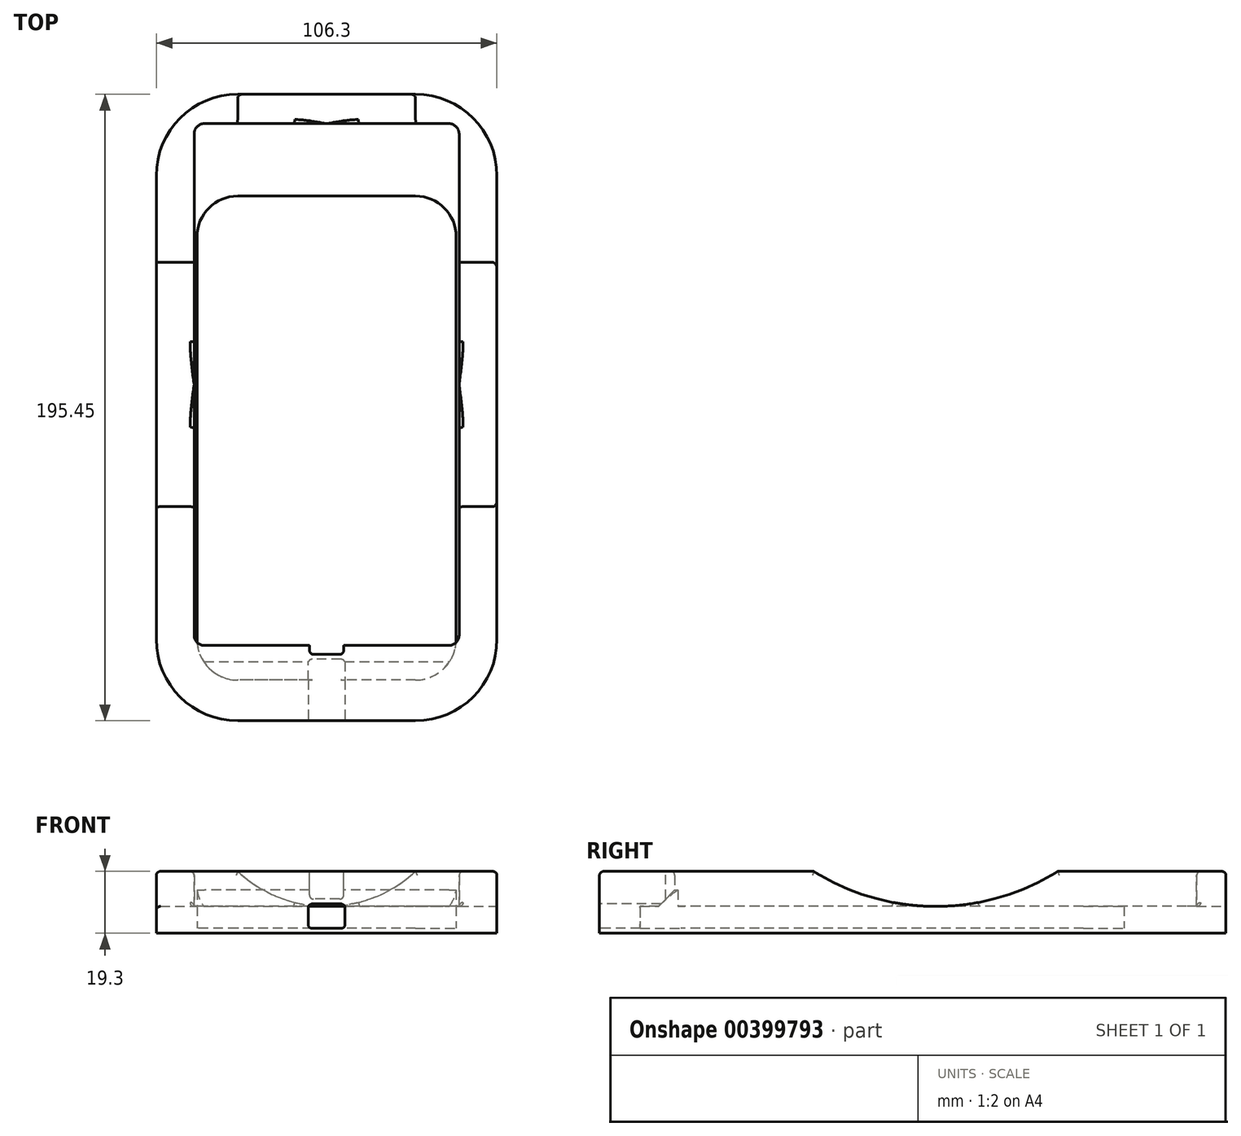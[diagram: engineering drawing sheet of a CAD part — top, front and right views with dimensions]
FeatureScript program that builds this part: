
annotation { "Feature Type Name" : "Feature", "Feature Type Description" : "" }
export const myFeature = defineFeature(function(context is Context, id is Id, definition is map)
    precondition{}
    {
        {
            var Q0;
            Q0=qCreatedBy(makeId("Top.planeOp"),FACE);
            var sketch = newSketch(context, id + "F0", { "sketchPlane" : qUnion([Q0])});
            skLineSegment(sketch, "E0.bottom", {"start": v(27.75, 75.5) * mm, "end": v(-27.75, 75.5) * mm});
            skLineSegment(sketch, "E0.top", {"start": v(27.75, -75.5) * mm, "end": v(-27.75, -75.5) * mm});
            skLineSegment(sketch, "E0.left", {"start": v(40.45, 62.8) * mm, "end": v(40.45, -62.8) * mm});
            skLineSegment(sketch, "E0.right", {"start": v(-40.45, 62.8) * mm, "end": v(-40.45, -62.8) * mm});
            skPoint(sketch, "E0.middle", {"position": v(0, 0) * mm});
            skPoint(sketch, "E1.visualSharp", {"position": v(40.45, 75.5) * mm});
            skArc(sketch, "E1.filletArc", {"start": v(40.45, 62.8) * mm, "mid": v(36.73, 71.78) * mm, "end": v(27.75, 75.5) * mm});
            skPoint(sketch, "E2.visualSharp", {"position": v(-40.45, 75.5) * mm});
            skArc(sketch, "E2.filletArc", {"start": v(-27.75, 75.5) * mm, "mid": v(-36.73, 71.78) * mm, "end": v(-40.45, 62.8) * mm});
            skPoint(sketch, "E3.visualSharp", {"position": v(-40.45, -75.5) * mm});
            skArc(sketch, "E3.filletArc", {"start": v(-40.45, -62.8) * mm, "mid": v(-36.73, -71.78) * mm, "end": v(-27.75, -75.5) * mm});
            skPoint(sketch, "E4.visualSharp", {"position": v(40.45, -75.5) * mm});
            skArc(sketch, "E4.filletArc", {"start": v(27.75, -75.5) * mm, "mid": v(36.73, -71.78) * mm, "end": v(40.45, -62.8) * mm});
            skLineSegment(sketch, "E5.0", {"start": v(-53.15, 81.85) * mm, "end": v(-53.15, -62.8) * mm});
            skLineSegment(sketch, "E5.1", {"start": v(53.15, 81.85) * mm, "end": v(53.15, -62.8) * mm});
            skArc(sketch, "E5.2", {"start": v(27.75, -88.2) * mm, "mid": v(45.71, -80.76) * mm, "end": v(53.15, -62.8) * mm});
            skLineSegment(sketch, "E5.3", {"start": v(27.75, -88.2) * mm, "end": v(-27.75, -88.2) * mm});
            skArc(sketch, "E5.4", {"start": v(-53.15, -62.8) * mm, "mid": v(-45.71, -80.76) * mm, "end": v(-27.75, -88.2) * mm});
            skLineSegment(sketch, "E6", {"start": v(-27.75, 107.25) * mm, "end": v(27.75, 107.25) * mm});
            skPoint(sketch, "E7.visualSharp", {"position": v(53.15, 107.25) * mm});
            skArc(sketch, "E7.filletArc", {"start": v(53.15, 81.85) * mm, "mid": v(45.71, 99.81) * mm, "end": v(27.75, 107.25) * mm});
            skPoint(sketch, "E8.visualSharp", {"position": v(-53.15, 107.25) * mm});
            skArc(sketch, "E8.filletArc", {"start": v(-27.75, 107.25) * mm, "mid": v(-45.71, 99.81) * mm, "end": v(-53.15, 81.85) * mm});
            skSolve(sketch);
        }
        {
            var Q0;
            Q0 = qSketchRegion(id + "F0", true);
            var Q1;
            Q1=makeQuery(id+"F0.imprint","IMPRINT",FACE,{"disambiguationData":[TD([[makeQuery(id+"F0.imprint","IMPRINT",EDGE,{"derivedFrom":sQuery(id+"F0.wireOp",EDGE,"E0.bottom")}),1.0]])]});
            extrude(context, id + "F1", {"entities" : qUnion([Q0, Q1]), "depth" : 1.52 * mm});
        }
        {
            var Q0;
            Q0=makeQuery(id+"F1.opExtrude","CAP_FACE",FACE,{"disambiguationData":[OSD([sQuery(id+"F0.wireOp",EDGE,"E5.0"),sQuery(id+"F0.wireOp",EDGE,"E5.1"),sQuery(id+"F0.wireOp",EDGE,"E5.2"),sQuery(id+"F0.wireOp",EDGE,"E5.3"),sQuery(id+"F0.wireOp",EDGE,"E5.4"),sQuery(id+"F0.wireOp",EDGE,"E6"),sQuery(id+"F0.wireOp",EDGE,"E7.filletArc"),sQuery(id+"F0.wireOp",EDGE,"E8.filletArc")])],"isStart":false});
            var sketch = newSketch(context, id + "F2", { "sketchPlane" : qUnion([Q0])});
            skLineSegment(sketch, "E9.0", {"start": v(27.75, 75.5) * mm, "end": v(-27.75, 75.5) * mm});
            skLineSegment(sketch, "E9.1", {"start": v(27.75, -75.5) * mm, "end": v(-27.75, -75.5) * mm});
            skLineSegment(sketch, "E9.2", {"start": v(40.45, 62.8) * mm, "end": v(40.45, -62.8) * mm});
            skLineSegment(sketch, "E9.3", {"start": v(-40.45, 62.8) * mm, "end": v(-40.45, -62.8) * mm});
            skPoint(sketch, "E9.4", {"position": v(0, 0) * mm});
            skPoint(sketch, "E9.5", {"position": v(40.45, 75.5) * mm});
            skArc(sketch, "E9.6", {"start": v(40.45, 62.8) * mm, "mid": v(36.73, 71.78) * mm, "end": v(27.75, 75.5) * mm});
            skPoint(sketch, "E9.7", {"position": v(-40.45, 75.5) * mm});
            skArc(sketch, "E9.8", {"start": v(-27.75, 75.5) * mm, "mid": v(-36.73, 71.78) * mm, "end": v(-40.45, 62.8) * mm});
            skPoint(sketch, "E9.9", {"position": v(-40.45, -75.5) * mm});
            skArc(sketch, "E9.10", {"start": v(-40.45, -62.8) * mm, "mid": v(-36.73, -71.78) * mm, "end": v(-27.75, -75.5) * mm});
            skPoint(sketch, "E9.11", {"position": v(40.45, -75.5) * mm});
            skArc(sketch, "E9.12", {"start": v(27.75, -75.5) * mm, "mid": v(36.73, -71.78) * mm, "end": v(40.45, -62.8) * mm});
            skLineSegment(sketch, "E9.13", {"start": v(-53.15, 81.85) * mm, "end": v(-53.15, -62.8) * mm});
            skLineSegment(sketch, "E9.14", {"start": v(53.15, 81.85) * mm, "end": v(53.15, -62.8) * mm});
            skArc(sketch, "E9.15", {"start": v(27.75, -88.2) * mm, "mid": v(45.71, -80.76) * mm, "end": v(53.15, -62.8) * mm});
            skLineSegment(sketch, "E9.16", {"start": v(27.75, -88.2) * mm, "end": v(-27.75, -88.2) * mm});
            skArc(sketch, "E9.17", {"start": v(-53.15, -62.8) * mm, "mid": v(-45.71, -80.76) * mm, "end": v(-27.75, -88.2) * mm});
            skLineSegment(sketch, "E9.18", {"start": v(-27.75, 107.25) * mm, "end": v(27.75, 107.25) * mm});
            skPoint(sketch, "E9.19", {"position": v(53.15, 107.25) * mm});
            skArc(sketch, "E9.20", {"start": v(53.15, 81.85) * mm, "mid": v(45.71, 99.81) * mm, "end": v(27.75, 107.25) * mm});
            skPoint(sketch, "E9.21", {"position": v(-53.15, 107.25) * mm});
            skArc(sketch, "E9.22", {"start": v(-27.75, 107.25) * mm, "mid": v(-45.71, 99.81) * mm, "end": v(-53.15, 81.85) * mm});
            skSolve(sketch);
        }
        {
            var Q0;
            Q0 = qSketchRegion(id + "F2", true);
            extrude(context, id + "F3", {"entities" : qUnion([Q0]), "operationType" : NewBodyOperationType.ADD, "depth" : 6.86 * mm});
        }
        {
            var Q0;
            Q0=makeQuery(id+"F3.opExtrude","CAP_FACE",FACE,{"disambiguationData":[OSD([sQuery(id+"F2.wireOp",EDGE,"E9.0"),sQuery(id+"F2.wireOp",EDGE,"E9.1"),sQuery(id+"F2.wireOp",EDGE,"E9.2"),sQuery(id+"F2.wireOp",EDGE,"E9.3"),sQuery(id+"F2.wireOp",EDGE,"E9.6"),sQuery(id+"F2.wireOp",EDGE,"E9.8"),sQuery(id+"F2.wireOp",EDGE,"E9.10"),sQuery(id+"F2.wireOp",EDGE,"E9.12"),sQuery(id+"F2.wireOp",EDGE,"E9.13"),sQuery(id+"F2.wireOp",EDGE,"E9.14"),sQuery(id+"F2.wireOp",EDGE,"E9.15"),sQuery(id+"F2.wireOp",EDGE,"E9.16"),sQuery(id+"F2.wireOp",EDGE,"E9.17"),sQuery(id+"F2.wireOp",EDGE,"E9.18"),sQuery(id+"F2.wireOp",EDGE,"E9.20"),sQuery(id+"F2.wireOp",EDGE,"E9.22")])],"isStart":false});
            var sketch = newSketch(context, id + "F4", { "sketchPlane" : qUnion([Q0])});
            skLineSegment(sketch, "E10.0", {"start": v(-27.75, 107.25) * mm, "end": v(27.75, 107.25) * mm});
            skArc(sketch, "E10.1", {"start": v(53.15, 81.85) * mm, "mid": v(45.71, 99.81) * mm, "end": v(27.75, 107.25) * mm});
            skLineSegment(sketch, "E10.2", {"start": v(53.15, 81.85) * mm, "end": v(53.15, -62.8) * mm});
            skArc(sketch, "E10.3", {"start": v(-27.75, 107.25) * mm, "mid": v(-45.71, 99.81) * mm, "end": v(-53.15, 81.85) * mm});
            skLineSegment(sketch, "E10.4", {"start": v(-53.15, 81.85) * mm, "end": v(-53.15, -62.8) * mm});
            skArc(sketch, "E10.5", {"start": v(-53.15, -62.8) * mm, "mid": v(-45.71, -80.76) * mm, "end": v(-27.75, -88.2) * mm});
            skLineSegment(sketch, "E10.6", {"start": v(27.75, -88.2) * mm, "end": v(-27.75, -88.2) * mm});
            skArc(sketch, "E10.7", {"start": v(27.75, -88.2) * mm, "mid": v(45.71, -80.76) * mm, "end": v(53.15, -62.8) * mm});
            skLineSegment(sketch, "E11.bottom", {"start": v(38.16, 98.1) * mm, "end": v(-38.16, 98.1) * mm});
            skLineSegment(sketch, "E11.top", {"start": v(38.16, -64.7) * mm, "end": v(-38.16, -64.7) * mm});
            skLineSegment(sketch, "E11.left", {"start": v(41.34, 94.93) * mm, "end": v(41.34, -61.53) * mm});
            skLineSegment(sketch, "E11.right", {"start": v(-41.34, 94.93) * mm, "end": v(-41.34, -61.53) * mm});
            skPoint(sketch, "E11.middle", {"position": v(0, 16.7) * mm});
            skPoint(sketch, "E12.visualSharp", {"position": v(-41.34, 98.1) * mm});
            skArc(sketch, "E12.filletArc", {"start": v(-38.16, 98.1) * mm, "mid": v(-40.4, 97.18) * mm, "end": v(-41.34, 94.93) * mm});
            skPoint(sketch, "E13.visualSharp", {"position": v(41.34, 98.1) * mm});
            skArc(sketch, "E13.filletArc", {"start": v(41.34, 94.93) * mm, "mid": v(40.4, 97.18) * mm, "end": v(38.16, 98.1) * mm});
            skArc(sketch, "E14.filletArc", {"start": v(-41.34, -61.53) * mm, "mid": v(-40.4, -63.78) * mm, "end": v(-38.16, -64.7) * mm});
            skPoint(sketch, "E15.visualSharp", {"position": v(41.34, -64.7) * mm});
            skArc(sketch, "E15.filletArc", {"start": v(38.16, -64.7) * mm, "mid": v(40.4, -63.78) * mm, "end": v(41.34, -61.53) * mm});
            skSolve(sketch);
        }
        {
            var Q0;
            Q0 = qSketchRegion(id + "F4", true);
            extrude(context, id + "F5", {"entities" : qUnion([Q0]), "operationType" : NewBodyOperationType.ADD, "depth" : 10.92 * mm});
        }
        {
            var Q0;
            Q0=makeQuery(id+"F5.opExtrude","CAP_EDGE",EDGE,{"disambiguationData":[OSD([sQuery(id+"F4.wireOp",EDGE,"E11.top")])],"isStart":true});
            chamfer(context, id + "F6", {"entities" : qUnion([Q0]), "width" : 5.08 * mm, "tangentPropagation" : true});
        }
        {
            var Q0;
            Q0=makeQuery(id+"F5.opExtrude","CAP_FACE",FACE,{"disambiguationData":[OSD([sQuery(id+"F4.wireOp",EDGE,"E10.0"),sQuery(id+"F4.wireOp",EDGE,"E10.1"),sQuery(id+"F4.wireOp",EDGE,"E10.2"),sQuery(id+"F4.wireOp",EDGE,"E10.3"),sQuery(id+"F4.wireOp",EDGE,"E10.4"),sQuery(id+"F4.wireOp",EDGE,"E10.5"),sQuery(id+"F4.wireOp",EDGE,"E10.6"),sQuery(id+"F4.wireOp",EDGE,"E10.7"),sQuery(id+"F4.wireOp",EDGE,"E11.bottom"),sQuery(id+"F4.wireOp",EDGE,"E11.top"),sQuery(id+"F4.wireOp",EDGE,"E11.left"),sQuery(id+"F4.wireOp",EDGE,"E11.right"),sQuery(id+"F4.wireOp",EDGE,"E12.filletArc"),sQuery(id+"F4.wireOp",EDGE,"E13.filletArc"),sQuery(id+"F4.wireOp",EDGE,"E14.filletArc"),sQuery(id+"F4.wireOp",EDGE,"E15.filletArc")])],"isStart":false});
            var sketch = newSketch(context, id + "F7", { "sketchPlane" : qUnion([Q0])});
            skLineSegment(sketch, "E16", {"start": v(0, 0) * mm, "end": v(0, -97.5) * mm, "construction": true});
            skPoint(sketch, "E16.endSnap0", {"position": v(0, -88.2) * mm});
            skLineSegment(sketch, "E17.bottom", {"start": v(5.33, -67.5) * mm, "end": v(-5.33, -67.5) * mm});
            skLineSegment(sketch, "E17.top", {"start": v(5.33, -44.94) * mm, "end": v(-5.33, -44.94) * mm});
            skLineSegment(sketch, "E17.left", {"start": v(5.33, -67.5) * mm, "end": v(5.33, -44.94) * mm});
            skLineSegment(sketch, "E17.right", {"start": v(-5.33, -67.5) * mm, "end": v(-5.33, -44.94) * mm});
            skPoint(sketch, "E17.middle", {"position": v(0, -56.22) * mm});
            skSolve(sketch);
        }
        {
            var Q0;
            Q0 = qSketchRegion(id + "F7", true);
            var Q1;
            Q1=makeQuery(id+"F1.opExtrude","CAP_FACE",FACE,{"disambiguationData":[OSD([sQuery(id+"F0.wireOp",EDGE,"E5.0"),sQuery(id+"F0.wireOp",EDGE,"E5.1"),sQuery(id+"F0.wireOp",EDGE,"E5.2"),sQuery(id+"F0.wireOp",EDGE,"E5.3"),sQuery(id+"F0.wireOp",EDGE,"E5.4"),sQuery(id+"F0.wireOp",EDGE,"E6"),sQuery(id+"F0.wireOp",EDGE,"E7.filletArc"),sQuery(id+"F0.wireOp",EDGE,"E8.filletArc")])],"isStart":false});
            extrude(context, id + "F8", {"entities" : qUnion([Q0]), "operationType" : NewBodyOperationType.REMOVE, "endBound" : BoundingType.UP_TO_SURFACE, "oppositeDirection" : true, "endBoundEntityFace" : qUnion([Q1]), "depth" : 25.4 * mm});
        }
        {
            var Q0;
            Q0=makeQuery(id+"F8.boolean.opBoolean","COPY",EDGE,{"derivedFrom":makeQuery(id+"F8.opExtrude","SWEPT_EDGE",EDGE,{"disambiguationData":[OSD([sQuery(id+"F7.wireOp",EDGE,"E17.bottom"),sQuery(id+"F7.wireOp",EDGE,"E17.left")])]})});
            var Q1;
            Q1=makeQuery(id+"F8.boolean.opBoolean","COPY",EDGE,{"derivedFrom":makeQuery(id+"F8.opExtrude","SWEPT_EDGE",EDGE,{"disambiguationData":[OSD([sQuery(id+"F7.wireOp",EDGE,"E17.bottom"),sQuery(id+"F7.wireOp",EDGE,"E17.right")])]})});
            fillet(context, id + "F9", {"entities" : qUnion([Q0, Q1]), "radius" : 1.27 * mm, "tangentPropagation" : true, "allowEdgeOverflow" : false});
        }
        {
            var Q0;
            Q0=makeQuery(id+"F5.boolean.opBoolean","MERGE",FACE,{"derivedFrom":[makeQuery(id+"F3.boolean.opBoolean","MERGE",FACE,{"derivedFrom":[makeQuery(id+"F1.opExtrude","SWEPT_FACE",FACE,{"disambiguationData":[OSD([sQuery(id+"F0.wireOp",EDGE,"E5.3")])]}),makeQuery(id+"F3.opExtrude","SWEPT_FACE",FACE,{"disambiguationData":[OSD([sQuery(id+"F2.wireOp",EDGE,"E9.16")])]})]}),makeQuery(id+"F5.opExtrude","SWEPT_FACE",FACE,{"disambiguationData":[OSD([sQuery(id+"F4.wireOp",EDGE,"E10.6")])]})]});
            var sketch = newSketch(context, id + "F10", { "sketchPlane" : qUnion([Q0])});
            skLineSegment(sketch, "E18.bottom", {"start": v(5.78, 9.14) * mm, "end": v(-5.78, 9.14) * mm});
            skLineSegment(sketch, "E18.top", {"start": v(5.78, 1.52) * mm, "end": v(-5.78, 1.52) * mm});
            skLineSegment(sketch, "E18.left", {"start": v(5.78, 9.14) * mm, "end": v(5.78, 1.52) * mm});
            skLineSegment(sketch, "E18.right", {"start": v(-5.78, 9.14) * mm, "end": v(-5.78, 1.52) * mm});
            skPoint(sketch, "E18.middle", {"position": v(0, 5.33) * mm});
            skLineSegment(sketch, "E19.0.0", {"start": v(-27.75, 1.52) * mm, "end": v(27.75, 1.52) * mm, "construction": true});
            skSolve(sketch);
        }
        {
            var Q0;
            Q0 = qSketchRegion(id + "F10", true);
            extrude(context, id + "F11", {"entities" : qUnion([Q0]), "operationType" : NewBodyOperationType.REMOVE, "oppositeDirection" : true, "depth" : 25.4 * mm});
        }
        {
            var Q0;
            Q0=makeQuery(id+"F11.boolean.opBoolean","COPY",EDGE,{"derivedFrom":makeQuery(id+"F11.opExtrude","SWEPT_EDGE",EDGE,{"disambiguationData":[OSD([sQuery(id+"F10.wireOp",EDGE,"E18.bottom"),sQuery(id+"F10.wireOp",EDGE,"E18.right")])]})});
            var Q1;
            Q1=makeQuery(id+"F11.boolean.opBoolean","COPY",EDGE,{"derivedFrom":makeQuery(id+"F11.opExtrude","SWEPT_EDGE",EDGE,{"disambiguationData":[OSD([sQuery(id+"F10.wireOp",EDGE,"E18.top"),sQuery(id+"F10.wireOp",EDGE,"E18.right")])]})});
            var Q2;
            Q2=makeQuery(id+"F11.boolean.opBoolean","COPY",EDGE,{"derivedFrom":makeQuery(id+"F11.opExtrude","SWEPT_EDGE",EDGE,{"disambiguationData":[OSD([sQuery(id+"F10.wireOp",EDGE,"E18.top"),sQuery(id+"F10.wireOp",EDGE,"E18.left")])]})});
            var Q3;
            Q3=makeQuery(id+"F11.boolean.opBoolean","COPY",EDGE,{"derivedFrom":makeQuery(id+"F11.opExtrude","SWEPT_EDGE",EDGE,{"disambiguationData":[OSD([sQuery(id+"F10.wireOp",EDGE,"E18.bottom"),sQuery(id+"F10.wireOp",EDGE,"E18.left")])]})});
            fillet(context, id + "F12", {"entities" : qUnion([Q0, Q1, Q2, Q3]), "radius" : 1.27 * mm, "tangentPropagation" : true, "allowEdgeOverflow" : false});
        }
        {
            var Q0;
            Q0=makeQuery(id+"F5.boolean.opBoolean","MERGE",FACE,{"derivedFrom":[makeQuery(id+"F3.boolean.opBoolean","MERGE",FACE,{"derivedFrom":[makeQuery(id+"F1.opExtrude","SWEPT_FACE",FACE,{"disambiguationData":[OSD([sQuery(id+"F0.wireOp",EDGE,"E5.1")])]}),makeQuery(id+"F3.opExtrude","SWEPT_FACE",FACE,{"disambiguationData":[OSD([sQuery(id+"F2.wireOp",EDGE,"E9.14")])]})]}),makeQuery(id+"F5.opExtrude","SWEPT_FACE",FACE,{"disambiguationData":[OSD([sQuery(id+"F4.wireOp",EDGE,"E10.2")])]})]});
            var sketch = newSketch(context, id + "F13", { "sketchPlane" : qUnion([Q0])});
            skPoint(sketch, "E20.0", {"position": v(16.7, 19.3) * mm});
            skCircle(sketch, "E21", {"center": v(16.7, 80.3) * mm, "radius": 71.91 * mm});
            skPoint(sketch, "E22.0", {"position": v(16.7, 8.38) * mm});
            skPoint(sketch, "E23", {"position": v(54.8, 19.3) * mm});
            skPoint(sketch, "E24", {"position": v(-21.4, 19.3) * mm});
            skSolve(sketch);
        }
        {
            var Q0;
            Q0 = qSketchRegion(id + "F13", true);
            extrude(context, id + "F14", {"entities" : qUnion([Q0]), "operationType" : NewBodyOperationType.REMOVE, "endBound" : BoundingType.THROUGH_ALL, "oppositeDirection" : true, "depth" : 25.4 * mm});
        }
        {
            var Q0;
            Q0=makeQuery(id+"F5.boolean.opBoolean","MERGE",FACE,{"derivedFrom":[makeQuery(id+"F3.boolean.opBoolean","MERGE",FACE,{"derivedFrom":[makeQuery(id+"F1.opExtrude","SWEPT_FACE",FACE,{"disambiguationData":[OSD([sQuery(id+"F0.wireOp",EDGE,"E6")])]}),makeQuery(id+"F3.opExtrude","SWEPT_FACE",FACE,{"disambiguationData":[OSD([sQuery(id+"F2.wireOp",EDGE,"E9.18")])]})]}),makeQuery(id+"F5.opExtrude","SWEPT_FACE",FACE,{"disambiguationData":[OSD([sQuery(id+"F4.wireOp",EDGE,"E10.0")])]})]});
            var sketch = newSketch(context, id + "F15", { "sketchPlane" : qUnion([Q0])});
            skCircle(sketch, "E25", {"center": v(0, 49.1) * mm, "radius": 40.71 * mm});
            skSolve(sketch);
        }
        {
            var Q0;
            Q0 = qSketchRegion(id + "F15", true);
            extrude(context, id + "F16", {"entities" : qUnion([Q0]), "operationType" : NewBodyOperationType.REMOVE, "oppositeDirection" : true, "depth" : 25.4 * mm});
        }
        {
            var Q0;
            {var subQ0=sQuery(id+"F4.wireOp",EDGE,"E12.filletArc");var subQ1=sQuery(id+"F4.wireOp",EDGE,"E11.right");Q0=makeQuery(id+"F14.boolean.opBoolean","SPLIT",EDGE,{"disambiguationData":[TD([makeQuery(id+"F5.opExtrude","SWEPT_FACE",FACE,{"disambiguationData":[OSD([subQ0])]})])],"derivedFrom":makeQuery(id+"F5.opExtrude","CAP_EDGE",EDGE,{"disambiguationData":[OSD([subQ1])],"isStart":false})});}
            var Q1;
            Q1=makeQuery(id+"F16.boolean.opBoolean","INTERSECT",EDGE,{"disambiguationData":[OD(1.0)],"derivedFrom":[makeQuery(id+"F5.opExtrude","SWEPT_FACE",FACE,{"disambiguationData":[OSD([sQuery(id+"F4.wireOp",EDGE,"E11.bottom")])]}),makeQuery(id+"F16.opExtrude","SWEPT_FACE",FACE,{"disambiguationData":[OSD([sQuery(id+"F15.wireOp",EDGE,"E25")])]})]});
            var Q2;
            Q2=makeQuery(id+"F16.boolean.opBoolean","COPY",EDGE,{"derivedFrom":makeQuery(id+"F16.opExtrude","CAP_EDGE",EDGE,{"disambiguationData":[OSD([sQuery(id+"F15.wireOp",EDGE,"E25")])],"isStart":true})});
            var Q3;
            Q3=makeQuery(id+"F5.opExtrude","CAP_EDGE",EDGE,{"disambiguationData":[OSD([sQuery(id+"F4.wireOp",EDGE,"E10.3")])],"isStart":false});
            var Q4;
            Q4=makeQuery(id+"F5.opExtrude","CAP_EDGE",EDGE,{"disambiguationData":[OSD([sQuery(id+"F4.wireOp",EDGE,"E10.1")])],"isStart":false});
            var Q5;
            {var subQ0=sQuery(id+"F4.wireOp",EDGE,"E13.filletArc");var subQ1=sQuery(id+"F4.wireOp",EDGE,"E11.bottom");Q5=makeQuery(id+"F16.boolean.opBoolean","SPLIT",EDGE,{"disambiguationData":[TD([makeQuery(id+"F5.opExtrude","SWEPT_FACE",FACE,{"disambiguationData":[OSD([subQ0])]})])],"derivedFrom":makeQuery(id+"F5.opExtrude","CAP_EDGE",EDGE,{"disambiguationData":[OSD([subQ1])],"isStart":false})});}
            var Q6;
            Q6=makeQuery(id+"F14.boolean.opBoolean","COPY",EDGE,{"derivedFrom":makeQuery(id+"F14.opExtrude","CAP_EDGE",EDGE,{"disambiguationData":[OSD([sQuery(id+"F13.wireOp",EDGE,"E21")])],"isStart":true})});
            var Q7;
            Q7=makeQuery(id+"F14.boolean.opBoolean","INTERSECT",EDGE,{"disambiguationData":[OD(0.0)],"derivedFrom":[makeQuery(id+"F5.opExtrude","SWEPT_FACE",FACE,{"disambiguationData":[OSD([sQuery(id+"F4.wireOp",EDGE,"E11.left")])]}),makeQuery(id+"F14.opExtrude","SWEPT_FACE",FACE,{"disambiguationData":[OSD([sQuery(id+"F13.wireOp",EDGE,"E21")])]})]});
            var Q8;
            Q8=makeQuery(id+"F14.boolean.opBoolean","INTERSECT",EDGE,{"disambiguationData":[OD(0.0)],"derivedFrom":[makeQuery(id+"F5.opExtrude","SWEPT_FACE",FACE,{"disambiguationData":[OSD([sQuery(id+"F4.wireOp",EDGE,"E11.right")])]}),makeQuery(id+"F14.opExtrude","SWEPT_FACE",FACE,{"disambiguationData":[OSD([sQuery(id+"F13.wireOp",EDGE,"E21")])]})]});
            var Q9;
            Q9=makeQuery(id+"F14.boolean.opBoolean","INTERSECT",EDGE,{"derivedFrom":[makeQuery(id+"F5.boolean.opBoolean","MERGE",FACE,{"derivedFrom":[makeQuery(id+"F3.boolean.opBoolean","MERGE",FACE,{"derivedFrom":[makeQuery(id+"F1.opExtrude","SWEPT_FACE",FACE,{"disambiguationData":[OSD([sQuery(id+"F0.wireOp",EDGE,"E5.0")])]}),makeQuery(id+"F3.opExtrude","SWEPT_FACE",FACE,{"disambiguationData":[OSD([sQuery(id+"F2.wireOp",EDGE,"E9.13")])]})]}),makeQuery(id+"F5.opExtrude","SWEPT_FACE",FACE,{"disambiguationData":[OSD([sQuery(id+"F4.wireOp",EDGE,"E10.4")])]})]}),makeQuery(id+"F14.opExtrude","SWEPT_FACE",FACE,{"disambiguationData":[OSD([sQuery(id+"F13.wireOp",EDGE,"E21")])]})]});
            var Q10;
            {var subQ0=sQuery(id+"F4.wireOp",EDGE,"E15.filletArc");var subQ1=sQuery(id+"F4.wireOp",EDGE,"E11.left");Q10=makeQuery(id+"F14.boolean.opBoolean","SPLIT",EDGE,{"disambiguationData":[TD([makeQuery(id+"F5.opExtrude","SWEPT_FACE",FACE,{"disambiguationData":[OSD([subQ0])]})])],"derivedFrom":makeQuery(id+"F5.opExtrude","CAP_EDGE",EDGE,{"disambiguationData":[OSD([subQ1])],"isStart":false})});}
            var Q11;
            {var subQ0=sQuery(id+"F4.wireOp",EDGE,"E14.filletArc");var subQ1=sQuery(id+"F4.wireOp",EDGE,"E11.right");Q11=makeQuery(id+"F14.boolean.opBoolean","SPLIT",EDGE,{"disambiguationData":[TD([makeQuery(id+"F5.opExtrude","SWEPT_FACE",FACE,{"disambiguationData":[OSD([subQ0])]})])],"derivedFrom":makeQuery(id+"F5.opExtrude","CAP_EDGE",EDGE,{"disambiguationData":[OSD([subQ1])],"isStart":false})});}
            var Q12;
            Q12=makeQuery(id+"F5.opExtrude","CAP_EDGE",EDGE,{"disambiguationData":[OSD([sQuery(id+"F4.wireOp",EDGE,"E10.5")])],"isStart":false});
            var Q13;
            Q13=makeQuery(id+"F8.boolean.opBoolean","COPY",EDGE,{"derivedFrom":makeQuery(id+"F8.opExtrude","CAP_EDGE",EDGE,{"disambiguationData":[OSD([sQuery(id+"F7.wireOp",EDGE,"E17.bottom")])],"isStart":true})});
            fillet(context, id + "F17", {"entities" : qUnion([Q0, Q1, Q2, Q3, Q4, Q5, Q6, Q7, Q8, Q9, Q10, Q11, Q12, Q13]), "radius" : 1.27 * mm, "tangentPropagation" : true, "allowEdgeOverflow" : false});
        }
    });
